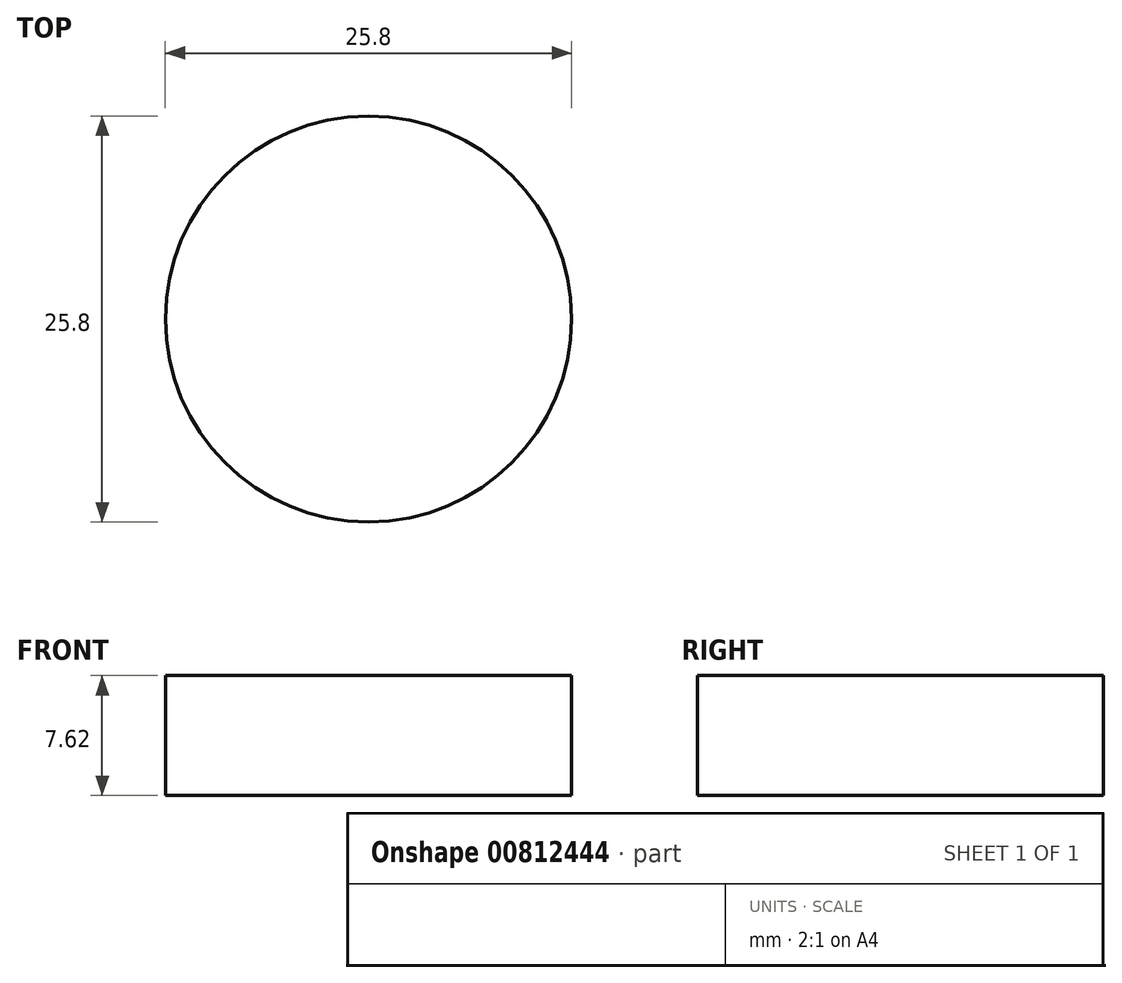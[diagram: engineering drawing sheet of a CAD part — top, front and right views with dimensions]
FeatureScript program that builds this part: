
annotation { "Feature Type Name" : "Feature", "Feature Type Description" : "" }
export const myFeature = defineFeature(function(context is Context, id is Id, definition is map)
    precondition{}
    {
        {
            var Q0;
            Q0=qCreatedBy(makeId("Top.planeOp"),FACE);
            var sketch = newSketch(context, id + "F0", { "sketchPlane" : qUnion([Q0])});
            skCircle(sketch, "E0", {"center": v(0, 0) * mm, "radius": 12.9 * mm});
            skSolve(sketch);
        }
        {
            var Q0;
            Q0 = qSketchRegion(id + "F0", true);
            extrude(context, id + "F1", {"entities" : qUnion([Q0]), "depth" : 7.62 * mm, "offsetDistance" : 25.4 * mm});
        }
    });
